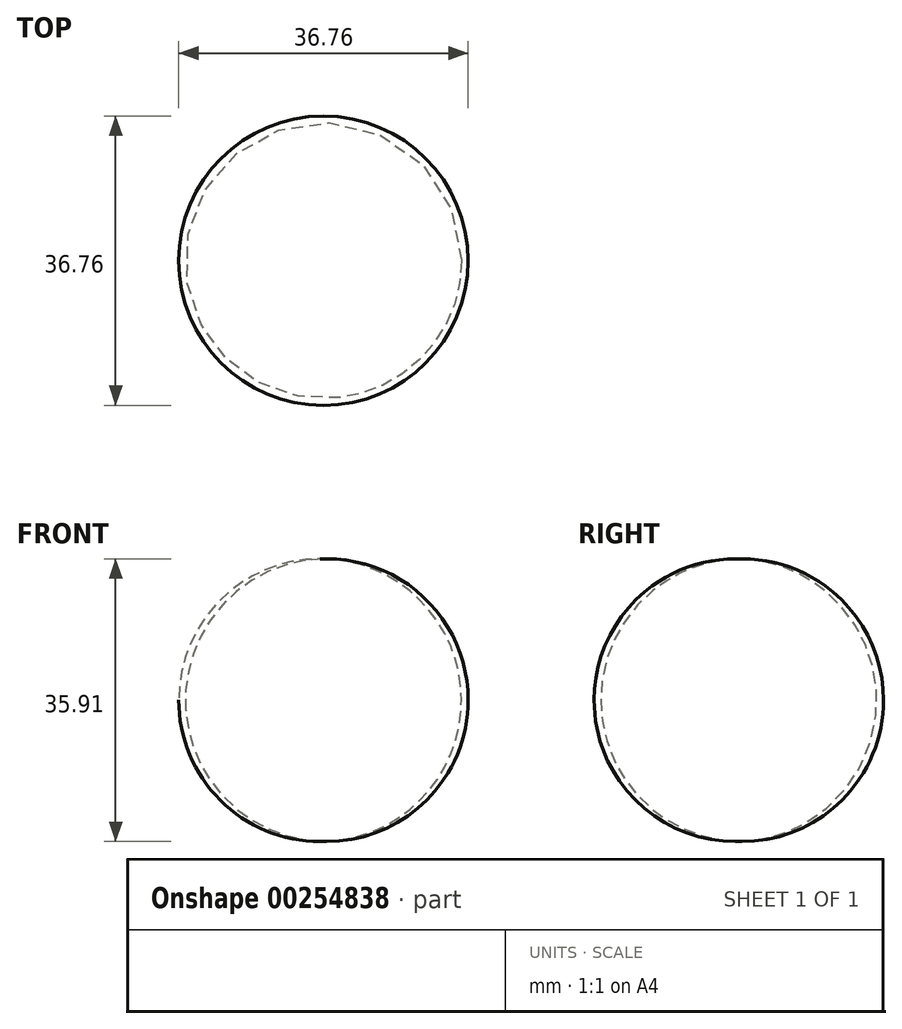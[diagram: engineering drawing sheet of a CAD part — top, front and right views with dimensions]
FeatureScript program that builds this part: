
annotation { "Feature Type Name" : "Feature", "Feature Type Description" : "" }
export const myFeature = defineFeature(function(context is Context, id is Id, definition is map)
    precondition{}
    {
        {
            var Q0;
            Q0=qCreatedBy(makeId("Front.planeOp"),FACE);
            var sketch = newSketch(context, id + "F0", { "sketchPlane" : qUnion([Q0])});
            skLineSegment(sketch, "E0", {"start": v(0, 0) * mm, "end": v(0, 35.9) * mm});
            skArc(sketch, "E1", {"start": v(0, 0) * mm, "mid": v(18.38, 17.95) * mm, "end": v(0, 35.9) * mm});
            skSolve(sketch);
        }
        {
            var Q0;
            Q0 = qSketchRegion(id + "F0", true);
            var Q1;
            Q1=sQuery(id+"F0.wireOp",EDGE,"E0");
            revolve(context, id + "F1", {"entities" : qUnion([Q0]), "axis" : qUnion([Q1]), "revolveType" : RevolveType.FULL});
        }
    });
